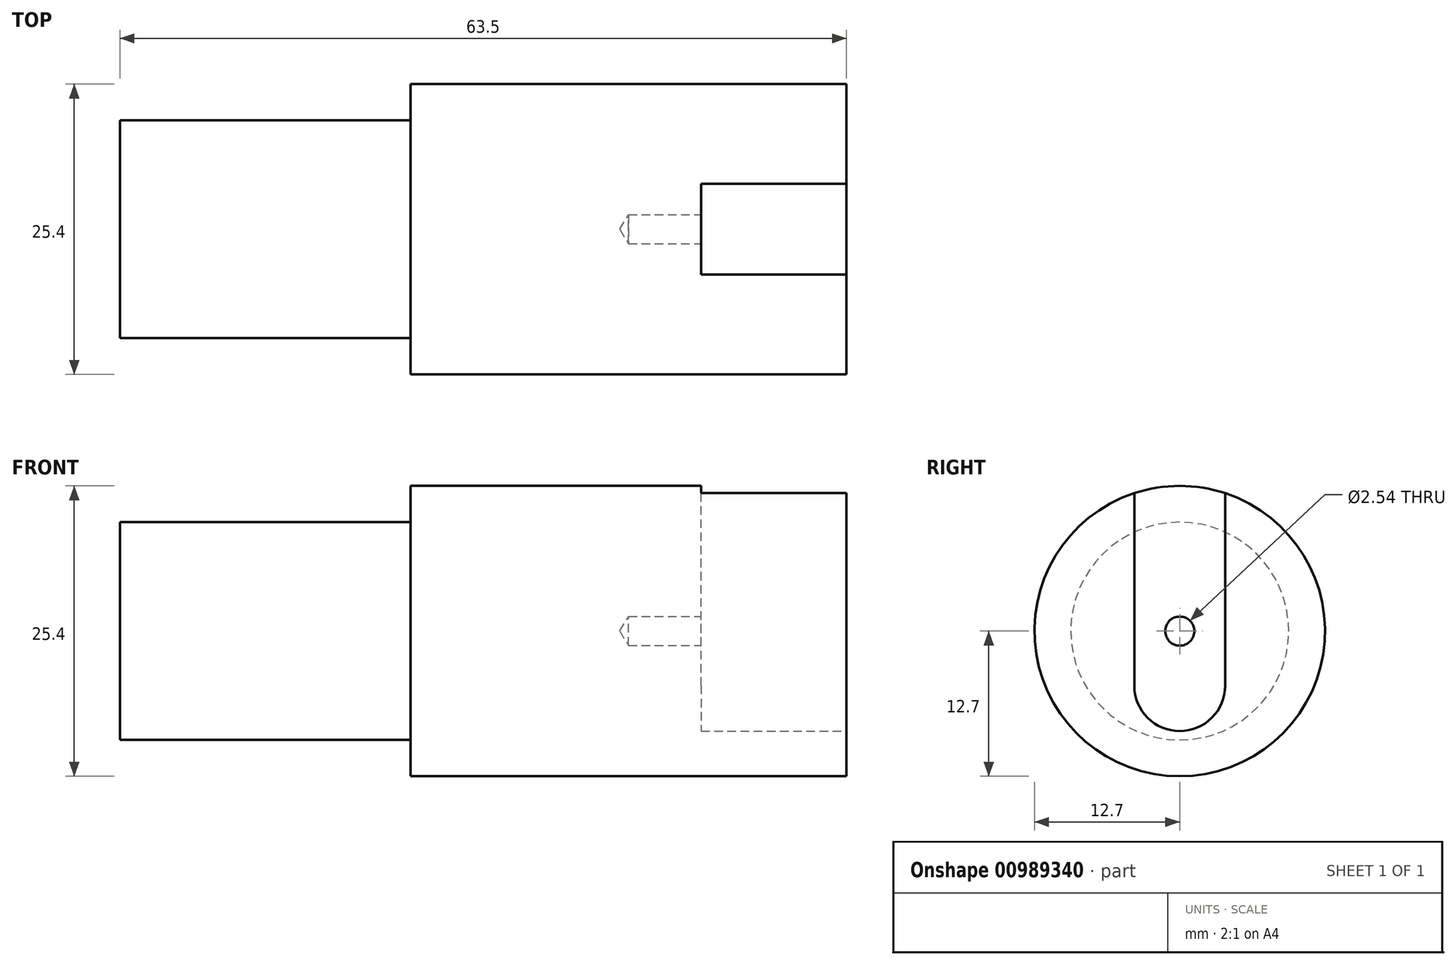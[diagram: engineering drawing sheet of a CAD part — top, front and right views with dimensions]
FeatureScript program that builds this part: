
annotation { "Feature Type Name" : "Feature", "Feature Type Description" : "" }
export const myFeature = defineFeature(function(context is Context, id is Id, definition is map)
    precondition{}
    {
        {
            var Q0;
            Q0=qCreatedBy(makeId("Right.planeOp"),FACE);
            var sketch = newSketch(context, id + "F0", { "sketchPlane" : qUnion([Q0])});
            skCircle(sketch, "E0", {"center": v(0, 0) * mm, "radius": 12.7 * mm});
            skSolve(sketch);
        }
        {
            var Q0;
            Q0 = qSketchRegion(id + "F0", true);
            extrude(context, id + "F1", {"entities" : qUnion([Q0]), "depth" : 25.4 * mm, "offsetDistance" : 25.4 * mm});
        }
        {
            var Q0;
            Q0=makeQuery(id+"F1.opExtrude","CAP_FACE",FACE,{"disambiguationData":[OSD([sQuery(id+"F0.wireOp",EDGE,"E0")])],"isStart":false});
            var sketch = newSketch(context, id + "F2", { "sketchPlane" : qUnion([Q0])});
            skArc(sketch, "E1", {"start": v(-3.98, 0) * mm, "mid": v(0, -3.98) * mm, "end": v(3.98, 0) * mm});
            skArc(sketch, "E2", {"start": v(-3.98, 12.06) * mm, "mid": v(0, -12.7) * mm, "end": v(3.98, 12.06) * mm});
            skLineSegment(sketch, "E3", {"start": v(3.98, 0) * mm, "end": v(3.98, 12.06) * mm});
            skLineSegment(sketch, "E4", {"start": v(-3.98, 0) * mm, "end": v(-3.98, 12.06) * mm});
            skSolve(sketch);
        }
        {
            var Q0;
            Q0 = qSketchRegion(id + "F2", true);
            extrude(context, id + "F3", {"entities" : qUnion([Q0]), "operationType" : NewBodyOperationType.ADD, "depth" : 12.7 * mm, "offsetDistance" : 25.4 * mm});
        }
        {
            var Q0;
            Q0=makeQuery(id+"F1.opExtrude","CAP_FACE",FACE,{"disambiguationData":[OSD([sQuery(id+"F0.wireOp",EDGE,"E0")])],"isStart":true});
            var sketch = newSketch(context, id + "F4", { "sketchPlane" : qUnion([Q0])});
            skCircle(sketch, "E5", {"center": v(0, 0) * mm, "radius": 9.53 * mm});
            skSolve(sketch);
        }
        {
            var Q0;
            Q0 = qSketchRegion(id + "F4", true);
            extrude(context, id + "F5", {"entities" : qUnion([Q0]), "operationType" : NewBodyOperationType.ADD, "depth" : 25.4 * mm, "offsetDistance" : 25.4 * mm});
        }
        {
            var Q0;
            Q0=makeQuery(id+"F1.opExtrude","CAP_FACE",FACE,{"disambiguationData":[OSD([sQuery(id+"F0.wireOp",EDGE,"E0")])],"isStart":false});
            var sketch = newSketch(context, id + "F6", { "sketchPlane" : qUnion([Q0])});
            skPoint(sketch, "E6", {"position": v(0, 0) * mm});
            skSolve(sketch);
        }
        {
            var Q0;
            Q0=sQuery(id+"F6.wireOp",VERTEX,"E6");
            var Q1;
            Q1=makeQuery(id+"F1.opExtrude","SWEPT_BODY",BODY,{"disambiguationData":[OSD([sQuery(id+"F0.wireOp",EDGE,"E0")])]});
            hole(context, id + "F7", {"style" : HoleStyle.SIMPLE, "endStyle" : HoleEndStyle.BLIND, "holeDiameter" : 2.54 * mm, "majorDiameter" : 6.35 * mm, "holeDepth" : 6.35 * mm, "isTappedThrough" : true, "tappedDepth" : 12.7 * mm, "tapClearance" : 3, "locations" : qUnion([Q0]), "scope" : qUnion([Q1])});
        }
        {
            var Q0;
            Q0=makeQuery(id+"F3.opExtrude","CAP_FACE",FACE,{"disambiguationData":[OSD([sQuery(id+"F2.wireOp",EDGE,"E1"),sQuery(id+"F2.wireOp",EDGE,"E2"),sQuery(id+"F2.wireOp",EDGE,"E3"),sQuery(id+"F2.wireOp",EDGE,"E4")])],"isStart":false});
            var sketch = newSketch(context, id + "F8", { "sketchPlane" : qUnion([Q0])});
            skArc(sketch, "E7", {"start": v(-3.98, -4.78) * mm, "mid": v(0, -8.75) * mm, "end": v(3.98, -4.78) * mm});
            skLineSegment(sketch, "E8", {"start": v(-3.98, 0) * mm, "end": v(-3.98, -4.78) * mm});
            skLineSegment(sketch, "E9", {"start": v(3.98, 0) * mm, "end": v(3.98, -4.78) * mm});
            skArc(sketch, "E10.0", {"start": v(-3.98, 0) * mm, "mid": v(0, -3.98) * mm, "end": v(3.98, 0) * mm});
            skSolve(sketch);
        }
        {
            var Q0;
            Q0=makeQuery(id+"F8.imprint","IMPRINT",FACE,{"disambiguationData":[TD([[makeQuery(id+"F8.imprint","IMPRINT",EDGE,{"derivedFrom":sQuery(id+"F8.wireOp",EDGE,"E7")}),1.0]])]});
            extrude(context, id + "F9", {"entities" : qUnion([Q0]), "oppositeDirection" : true, "depth" : 12.7 * mm, "offsetDistance" : 25.4 * mm});
        }
        {
            var Q0;
            Q0=makeQuery(id+"F9.opExtrude","SWEPT_BODY",BODY,{"disambiguationData":[OSD([sQuery(id+"F8.wireOp",EDGE,"E7"),sQuery(id+"F8.wireOp",EDGE,"E8"),sQuery(id+"F8.wireOp",EDGE,"E9"),sQuery(id+"F8.wireOp",EDGE,"E10.0")])]});
            var Q1;
            Q1=makeQuery(id+"F1.opExtrude","SWEPT_BODY",BODY,{"disambiguationData":[OSD([sQuery(id+"F0.wireOp",EDGE,"E0")])]});
            booleanBodies(context, id + "F10", {"operationType" : BooleanOperationType.SUBTRACTION, "tools" : qUnion([Q0]), "targets" : qUnion([Q1])});
        }
    });
